# Revit family: Shower-Wall_Mount_Handle-KOHLER-Composed-K-T97045BR_1
name_source: partatom
category: Specialty Equipment
revit_build: Autodesk Revit 2017 (Build: 20160225_1515(x64)
units: mm (PartAtom-declared; Revit-internal decimal feet)

## family parameters
Cut with Voids When Loaded = No
Host = Face
OmniClass Number = 23.31.25.00
OmniClass Title = Toilet and Bath Specialties
Part Type = Normal
Room Calculation Point = No
Round Connector Dimension = Use Diameter
Shared = No

## types (1)
- CP-Polished Chrome
    ADA Compliant = No
    Assembly Code = D2010
    Date Modified = 05/18/2021
    Default Elevation = 42"
    Description = Two-handle shower trim
    Finish = Kohler-Metal-CP-Polished_Chrome
    Handle Clearance = 1 1/2"
    Height = 2"
    Length = 1 7/16"
    Manufacturer = KOHLER Co.
    Master Format 2014 = 22 41 39
    Master Format 2014 Name = Residential Faucets, Supplies, and Trim
    Material = Premium Metal Construction
    Model = K-T97045BR-3-CP
    Product Name = Composed
    Type = 1
    URL = https://br.kohler.com
    WaterSense Certified = No

## geometry (parser evidence)
native form markers: Sweep x4
no freeform markers — native parametric forms only
